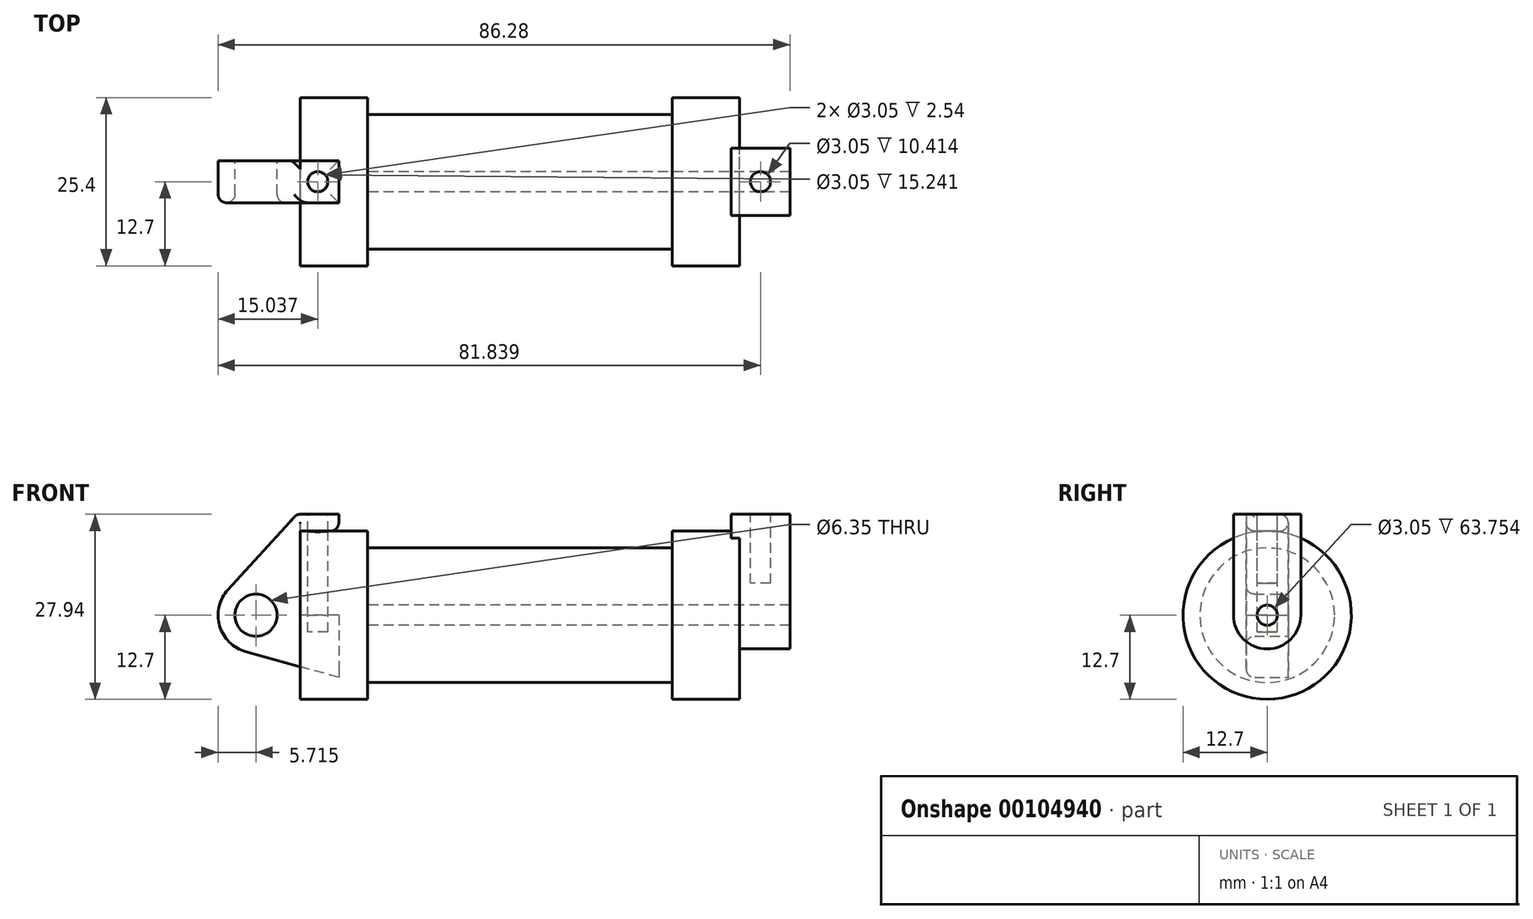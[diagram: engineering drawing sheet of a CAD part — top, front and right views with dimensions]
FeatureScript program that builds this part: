
annotation { "Feature Type Name" : "Feature", "Feature Type Description" : "" }
export const myFeature = defineFeature(function(context is Context, id is Id, definition is map)
    precondition{}
    {
        {
            var Q0;
            Q0=qCreatedBy(makeId("Front.planeOp"),FACE);
            var sketch = newSketch(context, id + "F0", { "sketchPlane" : qUnion([Q0])});
            skLineSegment(sketch, "E0", {"start": v(0, 0) * mm, "end": v(0, 12.7) * mm});
            skLineSegment(sketch, "E1", {"start": v(0, 12.7) * mm, "end": v(10.16, 12.7) * mm});
            skLineSegment(sketch, "E2", {"start": v(10.16, 12.7) * mm, "end": v(10.16, 10.16) * mm});
            skLineSegment(sketch, "E3", {"start": v(10.16, 10.16) * mm, "end": v(56.13, 10.16) * mm});
            skLineSegment(sketch, "E4", {"start": v(56.13, 10.16) * mm, "end": v(56.13, 12.7) * mm});
            skLineSegment(sketch, "E5", {"start": v(56.13, 12.7) * mm, "end": v(66.3, 12.7) * mm});
            skLineSegment(sketch, "E6", {"start": v(66.3, 12.7) * mm, "end": v(66.3, 0) * mm});
            skLineSegment(sketch, "E7", {"start": v(66.3, 0) * mm, "end": v(0, 0) * mm});
            skLineSegment(sketch, "E8", {"start": v(5.84, 15.24) * mm, "end": v(-0.5, 15.24) * mm});
            skLineSegment(sketch, "E9", {"start": v(-0.5, 15.24) * mm, "end": v(-10.88, 3.85) * mm});
            skLineSegment(sketch, "E10", {"start": v(0, 0) * mm, "end": v(-6.65, 0) * mm});
            skCircle(sketch, "E11", {"center": v(-6.65, 0) * mm, "radius": 5.72 * mm});
            skCircle(sketch, "E12", {"center": v(-6.65, 0) * mm, "radius": 3.18 * mm});
            skLineSegment(sketch, "E13", {"start": v(5.84, 15.24) * mm, "end": v(5.84, -9.4) * mm});
            skLineSegment(sketch, "E14", {"start": v(5.84, -9.4) * mm, "end": v(-8.18, -5.5) * mm});
            skSolve(sketch);
        }
        {
            var Q0;
            {var subQ0=sQuery(id+"F0.wireOp",EDGE,"E2");Q0=makeQuery(id+"F0.imprint","IMPRINT",FACE,{"disambiguationData":[TD([[makeQuery(id+"F0.imprint","IMPRINT",EDGE,{"derivedFrom":subQ0}),-1.0]])]});}
            var Q1;
            {var subQ0=sQuery(id+"F0.wireOp",EDGE,"E0");Q1=makeQuery(id+"F0.imprint","IMPRINT",FACE,{"disambiguationData":[TD([[makeQuery(id+"F0.imprint","IMPRINT",EDGE,{"derivedFrom":subQ0}),-1.0]])]});}
            var Q2;
            Q2=sQuery(id+"F0.wireOp",EDGE,"E7");
            revolve(context, id + "F1", {"entities" : qUnion([Q0, Q1]), "axis" : qUnion([Q2]), "revolveType" : RevolveType.FULL});
        }
        {
            var Q0;
            {var subQ3=sQuery(id+"F0.wireOp",EDGE,"E0");Q0=makeQuery(id+"F0.imprint","IMPRINT",FACE,{"disambiguationData":[TD([[makeQuery(id+"F0.imprint","IMPRINT",EDGE,{"derivedFrom":subQ3}),1.0]])]});}
            var Q1;
            {var subQ4=sQuery(id+"F0.wireOp",EDGE,"E12");Q1=makeQuery(id+"F0.imprint","IMPRINT",FACE,{"disambiguationData":[TD([[makeQuery(id+"F0.imprint","IMPRINT",EDGE,{"derivedFrom":subQ4}),-1.0]])]});}
            var Q2;
            {var subQ0=sQuery(id+"F0.wireOp",EDGE,"E14");Q2=makeQuery(id+"F0.imprint","IMPRINT",FACE,{"disambiguationData":[TD([[makeQuery(id+"F0.imprint","IMPRINT",EDGE,{"derivedFrom":subQ0}),-1.0]])]});}
            extrude(context, id + "F2", {"entities" : qUnion([Q0, Q1, Q2]), "endBound" : BoundingType.SYMMETRIC, "depth" : 6.35 * mm});
        }
        {
            var Q0;
            Q0=makeQuery(id+"F1.opRevolve","SWEPT_FACE",FACE,{"disambiguationData":[OSD([sQuery(id+"F0.wireOp",EDGE,"E6")])]});
            var sketch = newSketch(context, id + "F3", { "sketchPlane" : qUnion([Q0])});
            skCircle(sketch, "E15", {"center": v(0, 0) * mm, "radius": 1.52 * mm});
            skCircle(sketch, "E16", {"center": v(0, 0) * mm, "radius": 5.08 * mm});
            skLineSegment(sketch, "E17", {"start": v(-5.08, 0) * mm, "end": v(-5.08, 15.24) * mm});
            skLineSegment(sketch, "E18", {"start": v(5.08, 0) * mm, "end": v(5.08, 15.24) * mm});
            skLineSegment(sketch, "E19", {"start": v(-5.08, 15.24) * mm, "end": v(5.08, 15.24) * mm});
            skSolve(sketch);
        }
        {
            var Q0;
            {var subQ0=sQuery(id+"F3.wireOp",EDGE,"E17");var subQ1=sQuery(id+"F3.wireOp",EDGE,"E16");var subQ2=makeQuery(id+"F3.imprint","INTERSECT",VERTEX,{"derivedFrom":[subQ1,subQ0]});Q0=makeQuery(id+"F3.imprint","IMPRINT",FACE,{"disambiguationData":[TD([[makeQuery(id+"F3.imprint","IMPRINT",EDGE,{"disambiguationData":[TD([[subQ2,1.0]])],"derivedFrom":subQ1}),-1.0]])]});}
            var Q1;
            Q1=makeQuery(id+"F3.imprint","IMPRINT",FACE,{"disambiguationData":[TD([[makeQuery(id+"F3.imprint","IMPRINT",EDGE,{"derivedFrom":sQuery(id+"F3.wireOp",EDGE,"E15")}),-1.0]])]});
            extrude(context, id + "F4", {"entities" : qUnion([Q0, Q1]), "operationType" : NewBodyOperationType.ADD, "depth" : 7.62 * mm});
        }
        {
            var Q0;
            {var subQ0=sQuery(id+"F3.wireOp",EDGE,"E19");Q0=makeQuery(id+"F3.imprint","IMPRINT",FACE,{"disambiguationData":[TD([[makeQuery(id+"F3.imprint","IMPRINT",EDGE,{"derivedFrom":subQ0}),-1.0]])]});}
            extrude(context, id + "F5", {"entities" : qUnion([Q0]), "operationType" : NewBodyOperationType.ADD, "depth" : 7.62 * mm, "hasSecondDirection" : true, "secondDirectionOppositeDirection" : true, "secondDirectionDepth" : 1.27 * mm});
        }
        {
            var Q0;
            Q0=makeQuery(id+"F3.imprint","IMPRINT",FACE,{"disambiguationData":[TD([[makeQuery(id+"F3.imprint","IMPRINT",EDGE,{"derivedFrom":sQuery(id+"F3.wireOp",EDGE,"E15")}),1.0]])]});
            var Q1;
            Q1=makeQuery(id+"F1.opRevolve","SWEPT_FACE",FACE,{"disambiguationData":[OSD([sQuery(id+"F0.wireOp",EDGE,"E2")])]});
            extrude(context, id + "F6", {"entities" : qUnion([Q0]), "operationType" : NewBodyOperationType.REMOVE, "endBound" : BoundingType.UP_TO_SURFACE, "oppositeDirection" : true, "endBoundEntityFace" : qUnion([Q1]), "depth" : 25.4 * mm});
        }
        {
            var Q0;
            Q0=makeQuery(id+"F2.opExtrude","SWEPT_FACE",FACE,{"disambiguationData":[OSD([sQuery(id+"F0.wireOp",EDGE,"E8")])]});
            var sketch = newSketch(context, id + "F7", { "sketchPlane" : qUnion([Q0])});
            skLineSegment(sketch, "E20", {"start": v(5.84, -3.18) * mm, "end": v(-0.5, 3.18) * mm, "construction": true});
            skLineSegment(sketch, "E21", {"start": v(5.84, 3.18) * mm, "end": v(-0.5, -3.18) * mm, "construction": true});
            skCircle(sketch, "E22", {"center": v(2.67, 0) * mm, "radius": 1.52 * mm});
            skSolve(sketch);
        }
        {
            var Q0;
            Q0=makeQuery(id+"F7.imprint","IMPRINT",FACE,{"disambiguationData":[TD([[makeQuery(id+"F7.imprint","IMPRINT",EDGE,{"derivedFrom":sQuery(id+"F7.wireOp",EDGE,"E22")}),1.0]])]});
            extrude(context, id + "F8", {"entities" : qUnion([Q0]), "operationType" : NewBodyOperationType.REMOVE, "depth" : 17.78 * mm});
        }
        {
            var Q0;
            Q0=makeQuery(id+"F5.opExtrude","SWEPT_FACE",FACE,{"disambiguationData":[OSD([sQuery(id+"F3.wireOp",EDGE,"E19")])]});
            var sketch = newSketch(context, id + "F9", { "sketchPlane" : qUnion([Q0])});
            skLineSegment(sketch, "E23", {"start": v(73.91, 5.08) * mm, "end": v(65.02, -5.08) * mm, "construction": true});
            skLineSegment(sketch, "E24", {"start": v(65.02, 5.08) * mm, "end": v(73.91, -5.08) * mm, "construction": true});
            skCircle(sketch, "E25", {"center": v(69.47, 0) * mm, "radius": 1.52 * mm});
            skSolve(sketch);
        }
        {
            var Q0;
            Q0=makeQuery(id+"F9.imprint","IMPRINT",FACE,{"disambiguationData":[TD([[makeQuery(id+"F9.imprint","IMPRINT",EDGE,{"derivedFrom":sQuery(id+"F9.wireOp",EDGE,"E25")}),1.0]])]});
            var Q1;
            Q1=sQuery(id+"F9.wireOp",EDGE,"E24");
            var Q2;
            Q2=sQuery(id+"F9.wireOp",EDGE,"E23");
            extrude(context, id + "F10", {"entities" : qUnion([Q0]), "operationType" : NewBodyOperationType.REMOVE, "surfaceEntities" : qUnion([Q1, Q2]), "oppositeDirection" : true, "depth" : 10.4 * mm});
        }
        {
            var Q0;
            Q0=makeQuery(id+"F7.imprint","IMPRINT",FACE,{"disambiguationData":[TD([[makeQuery(id+"F7.imprint","IMPRINT",EDGE,{"derivedFrom":sQuery(id+"F7.wireOp",EDGE,"E22")}),1.0]])]});
            extrude(context, id + "F11", {"entities" : qUnion([Q0]), "operationType" : NewBodyOperationType.REMOVE, "oppositeDirection" : true, "depth" : 17.78 * mm});
        }
        {
            var Q0;
            Q0=makeQuery(id+"F1.opRevolve","SWEPT_EDGE",EDGE,{"disambiguationData":[OSD([sQuery(id+"F0.wireOp",EDGE,"E1"),sQuery(id+"F0.wireOp",EDGE,"E2")])]});
            var Q1;
            Q1=makeQuery(id+"F1.opRevolve","SWEPT_EDGE",EDGE,{"disambiguationData":[OSD([sQuery(id+"F0.wireOp",EDGE,"E2"),sQuery(id+"F0.wireOp",EDGE,"E3")])]});
            var Q2;
            Q2=makeQuery(id+"F1.opRevolve","SWEPT_EDGE",EDGE,{"disambiguationData":[OSD([sQuery(id+"F0.wireOp",EDGE,"E5"),sQuery(id+"F0.wireOp",EDGE,"E6")])]});
            var Q3;
            Q3=makeQuery(id+"F1.opRevolve","SWEPT_EDGE",EDGE,{"disambiguationData":[OSD([sQuery(id+"F0.wireOp",EDGE,"E4"),sQuery(id+"F0.wireOp",EDGE,"E5")])]});
            var Q4;
            Q4=makeQuery(id+"F5.opExtrude","CAP_EDGE",EDGE,{"disambiguationData":[OSD([sQuery(id+"F3.wireOp",EDGE,"E19")])],"isStart":false});
            var Q5;
            Q5=makeQuery(id+"F5.opExtrude","SWEPT_EDGE",EDGE,{"disambiguationData":[OSD([sQuery(id+"F3.wireOp",EDGE,"E17"),sQuery(id+"F3.wireOp",EDGE,"E19")])]});
            var Q6;
            Q6=makeQuery(id+"F5.opExtrude","CAP_EDGE",EDGE,{"disambiguationData":[OSD([sQuery(id+"F3.wireOp",EDGE,"E19")])],"isStart":true});
            var Q7;
            Q7=makeQuery(id+"F5.opExtrude","SWEPT_EDGE",EDGE,{"disambiguationData":[OSD([sQuery(id+"F3.wireOp",EDGE,"E18"),sQuery(id+"F3.wireOp",EDGE,"E19")])]});
            var Q8;
            Q8=makeQuery(id+"F10.boolean.opBoolean","COPY",EDGE,{"derivedFrom":makeQuery(id+"F10.opExtrude","CAP_EDGE",EDGE,{"disambiguationData":[OSD([sQuery(id+"F9.wireOp",EDGE,"E25")])],"isStart":true})});
            var Q9;
            Q9=makeQuery(id+"F4.opExtrude","CAP_EDGE",EDGE,{"disambiguationData":[OSD([sQuery(id+"F3.wireOp",EDGE,"E15")])],"isStart":false});
            var Q10;
            {var subQ0=sQuery(id+"F3.wireOp",EDGE,"E17");Q10=makeQuery(id+"F5.boolean.opBoolean","MERGE",EDGE,{"derivedFrom":[makeQuery(id+"F4.opExtrude","CAP_EDGE",EDGE,{"disambiguationData":[OSD([subQ0])],"isStart":false}),makeQuery(id+"F5.opExtrude","CAP_EDGE",EDGE,{"disambiguationData":[OSD([subQ0])],"isStart":false})]});}
            var Q11;
            Q11=makeQuery(id+"F4.opExtrude","SWEPT_FACE",FACE,{"disambiguationData":[OSD([sQuery(id+"F3.wireOp",EDGE,"E16")])]});
            var Q12;
            Q12=makeQuery(id+"F1.opRevolve","SWEPT_EDGE",EDGE,{"disambiguationData":[OSD([sQuery(id+"F0.wireOp",EDGE,"E0"),sQuery(id+"F0.wireOp",EDGE,"E1")])]});
            var Q13;
            Q13=makeQuery(id+"F2.opExtrude","CAP_EDGE",EDGE,{"disambiguationData":[OSD([sQuery(id+"F0.wireOp",EDGE,"E9")])],"isStart":false});
            var Q14;
            Q14=makeQuery(id+"F2.opExtrude","CAP_EDGE",EDGE,{"disambiguationData":[OSD([sQuery(id+"F0.wireOp",EDGE,"E11")])],"isStart":false});
            var Q15;
            Q15=makeQuery(id+"F2.opExtrude","CAP_EDGE",EDGE,{"disambiguationData":[OSD([sQuery(id+"F0.wireOp",EDGE,"E12")])],"isStart":false});
            var Q16;
            Q16=makeQuery(id+"F2.opExtrude","CAP_EDGE",EDGE,{"disambiguationData":[OSD([sQuery(id+"F0.wireOp",EDGE,"E8")])],"isStart":true});
            var Q17;
            Q17=makeQuery(id+"F2.opExtrude","SWEPT_EDGE",EDGE,{"disambiguationData":[OSD([sQuery(id+"F0.wireOp",EDGE,"E8"),sQuery(id+"F0.wireOp",EDGE,"E9")])]});
            var Q18;
            Q18=makeQuery(id+"F2.opExtrude","SWEPT_EDGE",EDGE,{"disambiguationData":[OSD([sQuery(id+"F0.wireOp",EDGE,"E1"),sQuery(id+"F0.wireOp",EDGE,"E13")])]});
            var Q19;
            Q19=makeQuery(id+"F2.opExtrude","CAP_EDGE",EDGE,{"disambiguationData":[OSD([sQuery(id+"F0.wireOp",EDGE,"E1")])],"isStart":false});
            var Q20;
            {var subQ0=sQuery(id+"F3.wireOp",EDGE,"E18");Q20=makeQuery(id+"F5.boolean.opBoolean","MERGE",EDGE,{"derivedFrom":[makeQuery(id+"F4.opExtrude","CAP_EDGE",EDGE,{"disambiguationData":[OSD([subQ0])],"isStart":false}),makeQuery(id+"F5.opExtrude","CAP_EDGE",EDGE,{"disambiguationData":[OSD([subQ0])],"isStart":false})]});}
            var Q21;
            Q21=makeQuery(id+"F4.opExtrude","CAP_EDGE",EDGE,{"disambiguationData":[OSD([sQuery(id+"F3.wireOp",EDGE,"E16")])],"isStart":false});
            var Q22;
            Q22=makeQuery(id+"F2.opExtrude","CAP_EDGE",EDGE,{"disambiguationData":[OSD([sQuery(id+"F0.wireOp",EDGE,"E1")])],"isStart":true});
            fillet(context, id + "F12", {"entities" : qUnion([Q0, Q1, Q2, Q3, Q4, Q5, Q6, Q7, Q8, Q9, Q10, Q11, Q12, Q13, Q14, Q15, Q16, Q17, Q18, Q19, Q20, Q21, Q22]), "radius" : 1.27 * mm, "tangentPropagation" : true, "allowEdgeOverflow" : false});
        }
    });
